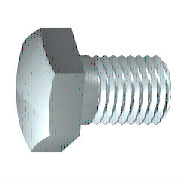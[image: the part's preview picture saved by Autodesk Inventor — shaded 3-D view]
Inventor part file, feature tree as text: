
AUTODESK INVENTOR PART (.ipt)
format: ipt  version: 2025.1 (Build 291241020, 241B)  size: 197,120 bytes
history: native  units: mm (DEFAULTED — no unit token found)
features: extrude x1, chamfer x1, plane x1
ambient origin geometry x7: Origin, YZ Plane, XZ Plane, X Axis, Y Axis, Z Axis, Center Point
bodies: Solid1 (feature_tree), Body (feature_tree)
feature tree (3):
  extrude  "Head"  Depth=30.0mm
  chamfer  "Chamfer1"  Distance=24.7mm
  plane  "Work Plane1"
